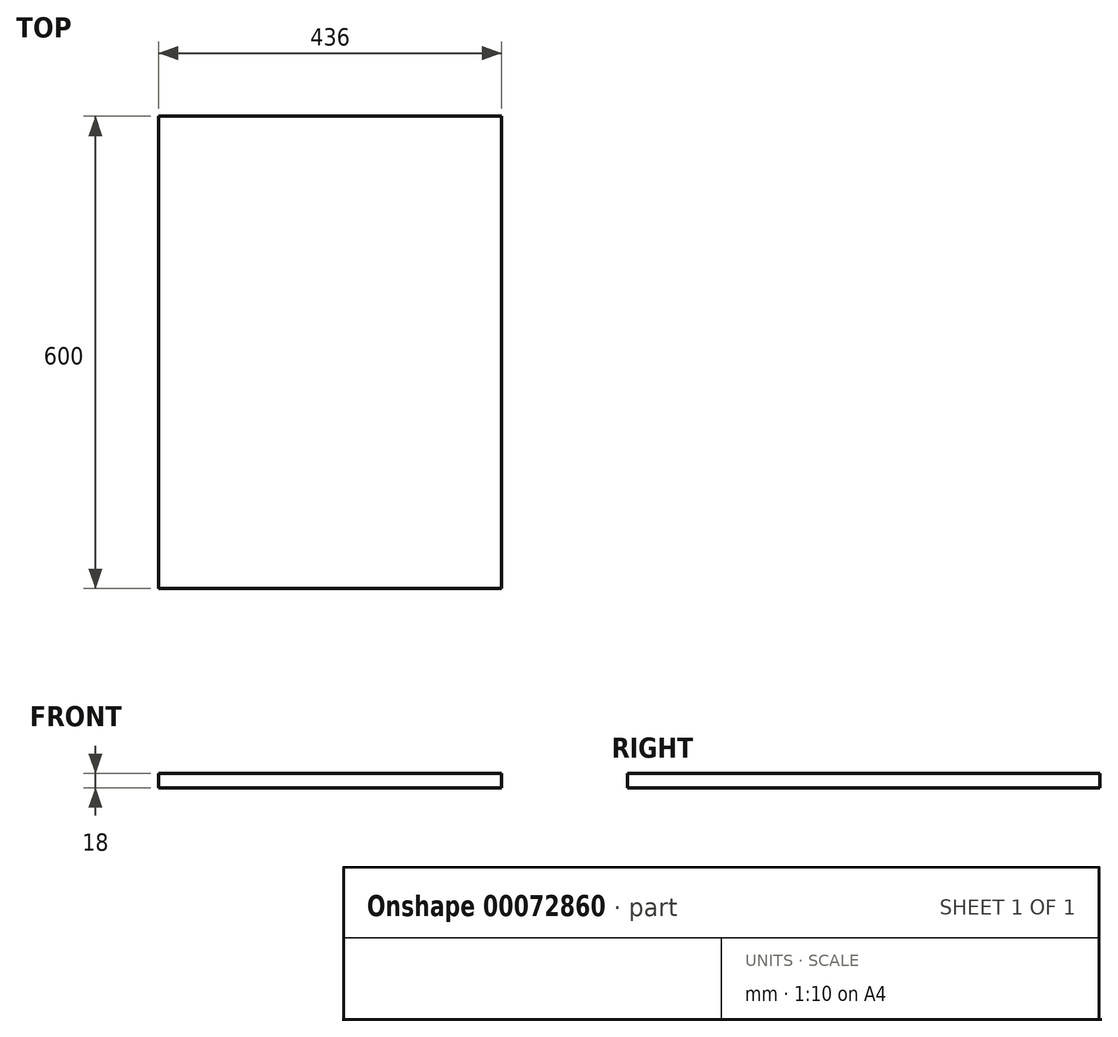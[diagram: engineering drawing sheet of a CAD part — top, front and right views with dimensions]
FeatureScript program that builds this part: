
annotation { "Feature Type Name" : "Feature", "Feature Type Description" : "" }
export const myFeature = defineFeature(function(context is Context, id is Id, definition is map)
    precondition{}
    {
        {
            var Q0;
            Q0=qCreatedBy(makeId("Top.planeOp"),FACE);
            var sketch = newSketch(context, id + "F0", { "sketchPlane" : qUnion([Q0])});
            skLineSegment(sketch, "E0.bottom", {"start": v(0, 0) * mm, "end": v(436, 0) * mm});
            skLineSegment(sketch, "E0.top", {"start": v(0, -600) * mm, "end": v(436, -600) * mm});
            skLineSegment(sketch, "E0.left", {"start": v(0, 0) * mm, "end": v(0, -600) * mm});
            skLineSegment(sketch, "E0.right", {"start": v(436, 0) * mm, "end": v(436, -600) * mm});
            skSolve(sketch);
        }
        {
            var Q0;
            Q0=makeQuery(id+"F0.imprint","IMPRINT",FACE,{"disambiguationData":[TD([[makeQuery(id+"F0.imprint","IMPRINT",EDGE,{"derivedFrom":sQuery(id+"F0.wireOp",EDGE,"E0.bottom")}),-1.0]])]});
            extrude(context, id + "F1", {"entities" : qUnion([Q0]), "depth" : 18 * mm});
        }
    });
